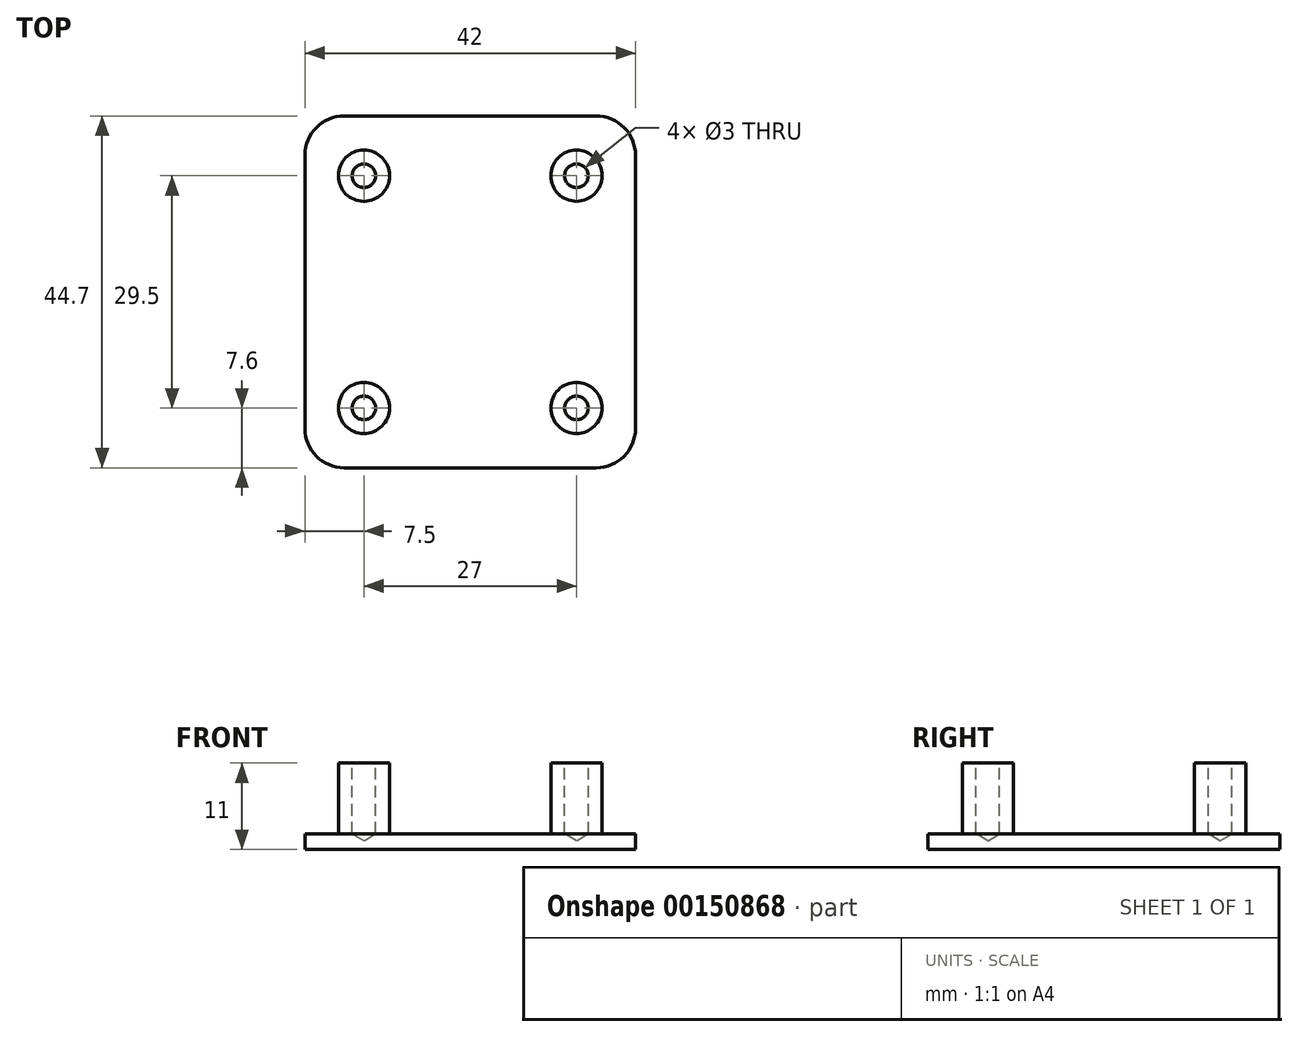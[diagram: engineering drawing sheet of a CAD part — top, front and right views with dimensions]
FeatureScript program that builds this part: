
annotation { "Feature Type Name" : "Feature", "Feature Type Description" : "" }
export const myFeature = defineFeature(function(context is Context, id is Id, definition is map)
    precondition{}
    {
        {
            var Q0;
            Q0=qCreatedBy(makeId("Top.planeOp"),FACE);
            var sketch = newSketch(context, id + "F0", { "sketchPlane" : qUnion([Q0])});
            skLineSegment(sketch, "E0.bottom", {"start": v(16, 22.35) * mm, "end": v(-16, 22.35) * mm});
            skLineSegment(sketch, "E0.top", {"start": v(16, -22.35) * mm, "end": v(-16, -22.35) * mm});
            skLineSegment(sketch, "E0.left", {"start": v(21, 17.35) * mm, "end": v(21, -17.35) * mm});
            skLineSegment(sketch, "E0.right", {"start": v(-21, 17.35) * mm, "end": v(-21, -17.35) * mm});
            skPoint(sketch, "E0.middle", {"position": v(0, 0) * mm});
            skPoint(sketch, "E1.visualSharp", {"position": v(21, 22.35) * mm});
            skArc(sketch, "E1.filletArc", {"start": v(21, 17.35) * mm, "mid": v(19.54, 20.89) * mm, "end": v(16, 22.35) * mm});
            skPoint(sketch, "E2.visualSharp", {"position": v(-21, 22.35) * mm});
            skArc(sketch, "E2.filletArc", {"start": v(-16, 22.35) * mm, "mid": v(-19.54, 20.89) * mm, "end": v(-21, 17.35) * mm});
            skPoint(sketch, "E3.visualSharp", {"position": v(-21, -22.35) * mm});
            skArc(sketch, "E3.filletArc", {"start": v(-21, -17.35) * mm, "mid": v(-19.54, -20.89) * mm, "end": v(-16, -22.35) * mm});
            skPoint(sketch, "E4.visualSharp", {"position": v(21, -22.35) * mm});
            skArc(sketch, "E4.filletArc", {"start": v(16, -22.35) * mm, "mid": v(19.54, -20.89) * mm, "end": v(21, -17.35) * mm});
            skSolve(sketch);
        }
        {
            var Q0;
            Q0=makeQuery(id+"F0.imprint","IMPRINT",FACE,{"disambiguationData":[TD([[makeQuery(id+"F0.imprint","IMPRINT",EDGE,{"derivedFrom":sQuery(id+"F0.wireOp",EDGE,"E0.bottom")}),1.0]])]});
            extrude(context, id + "F1", {"entities" : qUnion([Q0]), "depth" : 2 * mm});
        }
        {
            var Q0;
            Q0=makeQuery(id+"F1.opExtrude","CAP_FACE",FACE,{"disambiguationData":[OSD([sQuery(id+"F0.wireOp",EDGE,"E0.bottom"),sQuery(id+"F0.wireOp",EDGE,"E0.top"),sQuery(id+"F0.wireOp",EDGE,"E0.left"),sQuery(id+"F0.wireOp",EDGE,"E0.right"),sQuery(id+"F0.wireOp",EDGE,"E1.filletArc"),sQuery(id+"F0.wireOp",EDGE,"E2.filletArc"),sQuery(id+"F0.wireOp",EDGE,"E3.filletArc"),sQuery(id+"F0.wireOp",EDGE,"E4.filletArc")])],"isStart":false});
            var sketch = newSketch(context, id + "F2", { "sketchPlane" : qUnion([Q0])});
            skCircle(sketch, "E5", {"center": v(13.5, 14.75) * mm, "radius": 3.25 * mm});
            skCircle(sketch, "E6", {"center": v(-13.5, 14.75) * mm, "radius": 3.25 * mm});
            skCircle(sketch, "E7", {"center": v(13.5, -14.75) * mm, "radius": 3.25 * mm});
            skCircle(sketch, "E8", {"center": v(-13.5, -14.75) * mm, "radius": 3.25 * mm});
            skLineSegment(sketch, "E9", {"start": v(-13.5, 14.75) * mm, "end": v(13.5, 14.75) * mm, "construction": true});
            skLineSegment(sketch, "E10", {"start": v(-13.5, 14.75) * mm, "end": v(-13.5, -14.75) * mm, "construction": true});
            skPoint(sketch, "E11", {"position": v(0, 14.75) * mm});
            skPoint(sketch, "E12", {"position": v(-13.5, 0) * mm});
            skSolve(sketch);
        }
        {
            var Q0;
            Q0=makeQuery(id+"F2.imprint","IMPRINT",FACE,{"disambiguationData":[TD([[makeQuery(id+"F2.imprint","IMPRINT",EDGE,{"derivedFrom":sQuery(id+"F2.wireOp",EDGE,"E7")}),1.0]])]});
            var Q1;
            Q1=makeQuery(id+"F2.imprint","IMPRINT",FACE,{"disambiguationData":[TD([[makeQuery(id+"F2.imprint","IMPRINT",EDGE,{"derivedFrom":sQuery(id+"F2.wireOp",EDGE,"E6")}),1.0]])]});
            var Q2;
            Q2=makeQuery(id+"F2.imprint","IMPRINT",FACE,{"disambiguationData":[TD([[makeQuery(id+"F2.imprint","IMPRINT",EDGE,{"derivedFrom":sQuery(id+"F2.wireOp",EDGE,"E5")}),1.0]])]});
            var Q3;
            Q3=makeQuery(id+"F2.imprint","IMPRINT",FACE,{"disambiguationData":[TD([[makeQuery(id+"F2.imprint","IMPRINT",EDGE,{"derivedFrom":sQuery(id+"F2.wireOp",EDGE,"E8")}),1.0]])]});
            extrude(context, id + "F3", {"entities" : qUnion([Q0, Q1, Q2, Q3]), "operationType" : NewBodyOperationType.ADD, "depth" : 9 * mm});
        }
        {
            var Q0;
            Q0=makeQuery(id+"F3.opExtrude","CAP_FACE",FACE,{"disambiguationData":[OSD([sQuery(id+"F2.wireOp",EDGE,"E8")])],"isStart":false});
            var sketch = newSketch(context, id + "F4", { "sketchPlane" : qUnion([Q0])});
            skPoint(sketch, "E13", {"position": v(-13.5, 14.75) * mm});
            skPoint(sketch, "E14", {"position": v(13.5, 14.75) * mm});
            skPoint(sketch, "E15", {"position": v(-13.5, -14.75) * mm});
            skPoint(sketch, "E16", {"position": v(13.5, -14.75) * mm});
            skSolve(sketch);
        }
        {
            var Q0;
            Q0=sQuery(id+"F4.wireOp",VERTEX,"E13");
            var Q1;
            Q1=sQuery(id+"F4.wireOp",VERTEX,"E14");
            var Q2;
            Q2=sQuery(id+"F4.wireOp",VERTEX,"E16");
            var Q3;
            Q3=sQuery(id+"F4.wireOp",VERTEX,"E15");
            var Q4;
            Q4=makeQuery(id+"F1.opExtrude","SWEPT_BODY",BODY,{"disambiguationData":[OSD([sQuery(id+"F0.wireOp",EDGE,"E0.bottom"),sQuery(id+"F0.wireOp",EDGE,"E0.top"),sQuery(id+"F0.wireOp",EDGE,"E0.left"),sQuery(id+"F0.wireOp",EDGE,"E0.right"),sQuery(id+"F0.wireOp",EDGE,"E1.filletArc"),sQuery(id+"F0.wireOp",EDGE,"E2.filletArc"),sQuery(id+"F0.wireOp",EDGE,"E3.filletArc"),sQuery(id+"F0.wireOp",EDGE,"E4.filletArc")])]});
            hole(context, id + "F5", {"style" : HoleStyle.SIMPLE, "endStyle" : HoleEndStyle.BLIND, "holeDiameter" : 3 * mm, "holeDepth" : 9 * mm, "locations" : qUnion([Q0, Q1, Q2, Q3]), "scope" : qUnion([Q4])});
        }
    });
